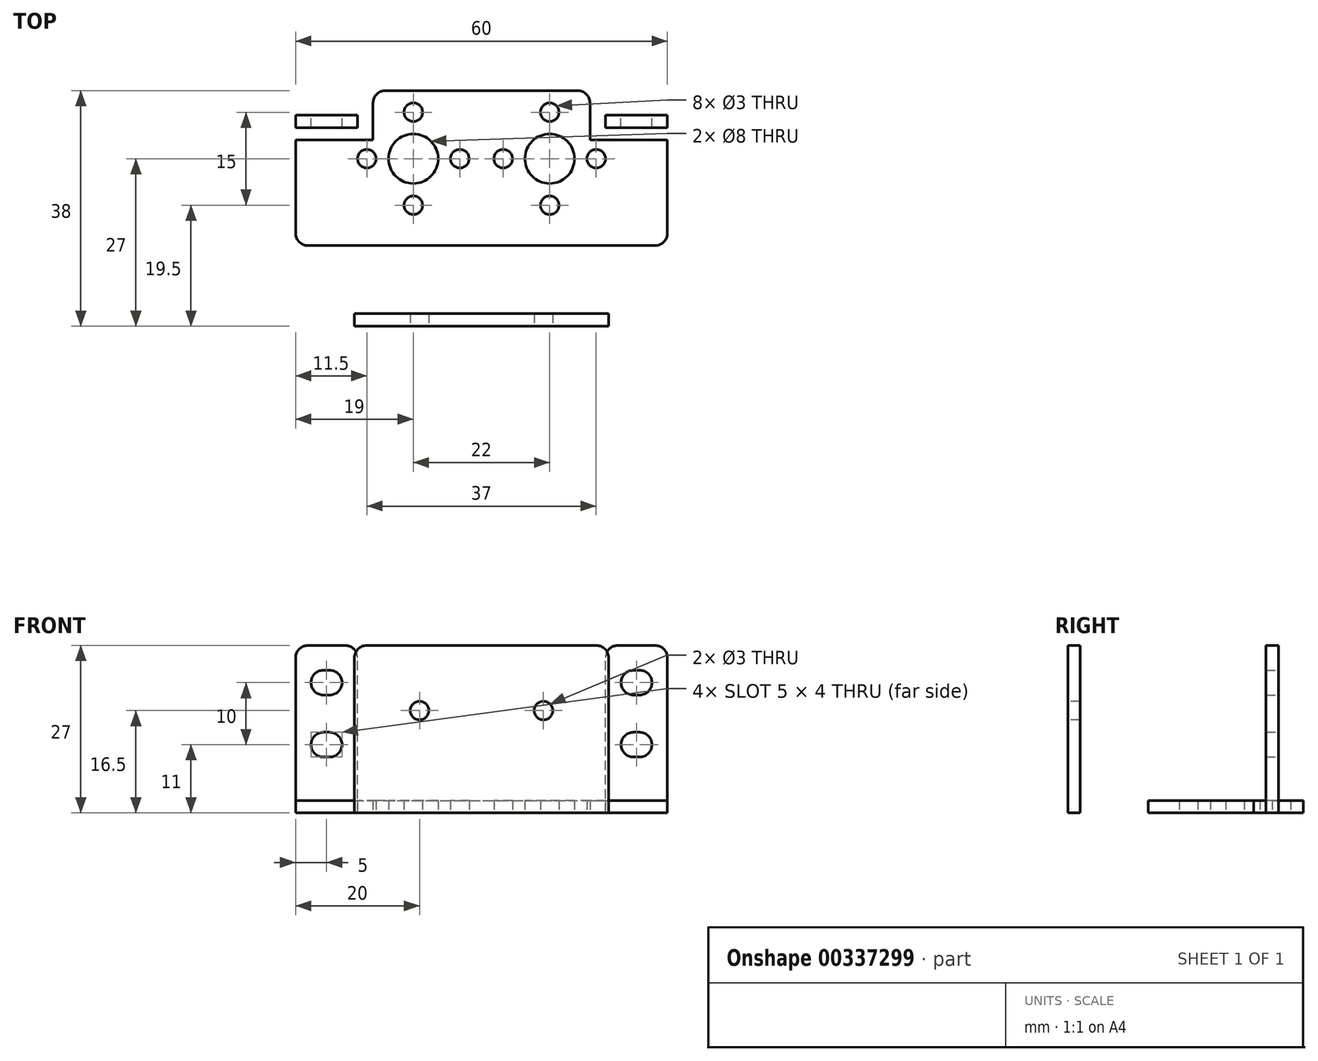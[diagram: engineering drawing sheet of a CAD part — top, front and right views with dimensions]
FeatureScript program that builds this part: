
annotation { "Feature Type Name" : "Feature", "Feature Type Description" : "" }
export const myFeature = defineFeature(function(context is Context, id is Id, definition is map)
    precondition{}
    {
        {
            var Q0;
            Q0=qCreatedBy(makeId("Top.planeOp"),FACE);
            var sketch = newSketch(context, id + "F0", { "sketchPlane" : qUnion([Q0])});
            skLineSegment(sketch, "E0.bottom", {"start": v(-17.5, 25) * mm, "end": v(17.5, 25) * mm});
            skLineSegment(sketch, "E0.top", {"start": v(-17.5, 17) * mm, "end": v(17.5, 17) * mm});
            skLineSegment(sketch, "E0.left", {"start": v(-17.5, 25) * mm, "end": v(-17.5, 17) * mm});
            skLineSegment(sketch, "E0.right", {"start": v(17.5, 25) * mm, "end": v(17.5, 17) * mm});
            skLineSegment(sketch, "E1.bottom", {"start": v(-30, 17) * mm, "end": v(30, 17) * mm});
            skLineSegment(sketch, "E1.top", {"start": v(-30, 0) * mm, "end": v(30, 0) * mm});
            skLineSegment(sketch, "E1.left", {"start": v(-30, 17) * mm, "end": v(-30, 0) * mm});
            skLineSegment(sketch, "E1.right", {"start": v(30, 17) * mm, "end": v(30, 0) * mm});
            skLineSegment(sketch, "E2.bottom", {"start": v(-20.5, 0) * mm, "end": v(20.5, 0) * mm});
            skLineSegment(sketch, "E2.top", {"start": v(-20.5, -13) * mm, "end": v(20.5, -13) * mm});
            skLineSegment(sketch, "E2.left", {"start": v(-20.5, 0) * mm, "end": v(-20.5, -13) * mm});
            skLineSegment(sketch, "E2.right", {"start": v(20.5, 0) * mm, "end": v(20.5, -13) * mm});
            skLineSegment(sketch, "E3.bottom", {"start": v(-30, 17) * mm, "end": v(-20, 17) * mm});
            skLineSegment(sketch, "E3.top", {"start": v(-30, 21) * mm, "end": v(-20, 21) * mm});
            skLineSegment(sketch, "E3.left", {"start": v(-30, 17) * mm, "end": v(-30, 21) * mm});
            skLineSegment(sketch, "E3.right", {"start": v(-20, 17) * mm, "end": v(-20, 21) * mm});
            skLineSegment(sketch, "E4.bottom", {"start": v(30, 17) * mm, "end": v(20, 17) * mm});
            skLineSegment(sketch, "E4.top", {"start": v(30, 21) * mm, "end": v(20, 21) * mm});
            skLineSegment(sketch, "E4.left", {"start": v(30, 17) * mm, "end": v(30, 21) * mm});
            skLineSegment(sketch, "E4.right", {"start": v(20, 17) * mm, "end": v(20, 21) * mm});
            skCircle(sketch, "E5", {"center": v(-11, 14) * mm, "radius": 4 * mm});
            skCircle(sketch, "E6", {"center": v(-11, 21.5) * mm, "radius": 1.5 * mm});
            skCircle(sketch, "E7", {"center": v(-3.5, 14) * mm, "radius": 1.5 * mm});
            skCircle(sketch, "E8", {"center": v(-11, 6.5) * mm, "radius": 1.5 * mm});
            skCircle(sketch, "E9", {"center": v(-18.5, 14) * mm, "radius": 1.5 * mm});
            skCircle(sketch, "E10", {"center": v(11, 14) * mm, "radius": 4 * mm});
            skCircle(sketch, "E11", {"center": v(11, 21.5) * mm, "radius": 1.5 * mm});
            skCircle(sketch, "E12", {"center": v(18.5, 14) * mm, "radius": 1.5 * mm});
            skCircle(sketch, "E13", {"center": v(11, 6.5) * mm, "radius": 1.5 * mm});
            skCircle(sketch, "E14", {"center": v(3.5, 14) * mm, "radius": 1.5 * mm});
            skPoint(sketch, "E15", {"position": v(0, 25) * mm});
            skSolve(sketch);
        }
        {
            var Q0;
            Q0=sQuery(id+"F0.wireOp",EDGE,"E2.top");
            var Q1;
            Q1=qCreatedBy(makeId("Front.planeOp"),FACE);
            cPlane(context, id + "F1", {"entities" : qUnion([Q0, Q1]), "cplaneType" : CPlaneType.LINE_ANGLE, "offset" : 25.4 * mm, "angle" : 0 * degree, "width" : 152.4 * mm, "height" : 152.4 * mm});
        }
        {
            var Q0;
            Q0=sQuery(id+"F0.wireOp",EDGE,"E4.top");
            var Q1;
            Q1=qCreatedBy(makeId("Front.planeOp"),FACE);
            cPlane(context, id + "F2", {"entities" : qUnion([Q0, Q1]), "cplaneType" : CPlaneType.LINE_ANGLE, "offset" : 25.4 * mm, "angle" : 0 * degree, "width" : 152.4 * mm, "height" : 152.4 * mm});
        }
        {
            var Q0;
            Q0=sQuery(id+"F0.wireOp",EDGE,"E3.top");
            var Q1;
            Q1=qCreatedBy(makeId("Front.planeOp"),FACE);
            cPlane(context, id + "F3", {"entities" : qUnion([Q0, Q1]), "cplaneType" : CPlaneType.LINE_ANGLE, "offset" : 25.4 * mm, "angle" : 0 * degree, "width" : 152.4 * mm, "height" : 152.4 * mm});
        }
        {
            var Q0;
            Q0=qCreatedBy(id+"F1.planeOp",FACE);
            var sketch = newSketch(context, id + "F4", { "sketchPlane" : qUnion([Q0])});
            skLineSegment(sketch, "E16.bottom", {"start": v(20.5, 0) * mm, "end": v(-20.5, 0) * mm});
            skLineSegment(sketch, "E16.top", {"start": v(20.5, 27) * mm, "end": v(-20.5, 27) * mm});
            skLineSegment(sketch, "E16.left", {"start": v(20.5, 0) * mm, "end": v(20.5, 27) * mm});
            skLineSegment(sketch, "E16.right", {"start": v(-20.5, 0) * mm, "end": v(-20.5, 27) * mm});
            skCircle(sketch, "E17", {"center": v(10, 16.5) * mm, "radius": 1.5 * mm});
            skCircle(sketch, "E18.MirrorC", {"center": v(-10, 16.5) * mm, "radius": 1.5 * mm});
            skSolve(sketch);
        }
        {
            var Q0;
            Q0=qCreatedBy(id+"F2.planeOp",FACE);
            var sketch = newSketch(context, id + "F5", { "sketchPlane" : qUnion([Q0])});
            skLineSegment(sketch, "E19.bottom", {"start": v(-30, 0) * mm, "end": v(-20, 0) * mm});
            skLineSegment(sketch, "E19.top", {"start": v(-30, 27) * mm, "end": v(-20, 27) * mm});
            skLineSegment(sketch, "E19.left", {"start": v(-30, 0) * mm, "end": v(-30, 27) * mm});
            skLineSegment(sketch, "E19.right", {"start": v(-20, 0) * mm, "end": v(-20, 27) * mm});
            skLineSegment(sketch, "E20.bottom", {"start": v(-25.5, 23) * mm, "end": v(-24.5, 23) * mm});
            skLineSegment(sketch, "E20.top", {"start": v(-25.5, 19) * mm, "end": v(-24.5, 19) * mm});
            skLineSegment(sketch, "E20.left", {"start": v(-25.5, 23) * mm, "end": v(-25.5, 19) * mm});
            skLineSegment(sketch, "E20.right", {"start": v(-24.5, 23) * mm, "end": v(-24.5, 19) * mm});
            skArc(sketch, "E21", {"start": v(-25.5, 23) * mm, "mid": v(-27.5, 21) * mm, "end": v(-25.5, 19) * mm});
            skArc(sketch, "E22", {"start": v(-24.5, 19) * mm, "mid": v(-22.5, 21) * mm, "end": v(-24.5, 23) * mm});
            skPoint(sketch, "E23", {"position": v(-25, 21) * mm});
            skPoint(sketch, "E24", {"position": v(-25, 27) * mm});
            skPoint(sketch, "E25", {"position": v(-25, 23) * mm});
            skLineSegment(sketch, "E26.bottom", {"start": v(-25.5, 13) * mm, "end": v(-24.5, 13) * mm});
            skLineSegment(sketch, "E26.top", {"start": v(-25.5, 9) * mm, "end": v(-24.5, 9) * mm});
            skLineSegment(sketch, "E26.left", {"start": v(-25.5, 13) * mm, "end": v(-25.5, 9) * mm});
            skLineSegment(sketch, "E26.right", {"start": v(-24.5, 13) * mm, "end": v(-24.5, 9) * mm});
            skArc(sketch, "E27", {"start": v(-25.5, 13) * mm, "mid": v(-27.5, 11) * mm, "end": v(-25.5, 9) * mm});
            skArc(sketch, "E28", {"start": v(-24.5, 9) * mm, "mid": v(-22.5, 11) * mm, "end": v(-24.5, 13) * mm});
            skPoint(sketch, "E29", {"position": v(-25, 11) * mm});
            skPoint(sketch, "E30", {"position": v(-25, 13) * mm});
            skSolve(sketch);
        }
        {
            var Q0;
            Q0=qCreatedBy(id+"F3.planeOp",FACE);
            var sketch = newSketch(context, id + "F6", { "sketchPlane" : qUnion([Q0])});
            skLineSegment(sketch, "E31.bottom", {"start": v(20, 0) * mm, "end": v(30, 0) * mm});
            skLineSegment(sketch, "E31.top", {"start": v(20, 27) * mm, "end": v(30, 27) * mm});
            skLineSegment(sketch, "E31.left", {"start": v(20, 0) * mm, "end": v(20, 27) * mm});
            skLineSegment(sketch, "E31.right", {"start": v(30, 0) * mm, "end": v(30, 27) * mm});
            skLineSegment(sketch, "E32.bottom", {"start": v(24.5, 23) * mm, "end": v(25.5, 23) * mm});
            skLineSegment(sketch, "E32.top", {"start": v(24.5, 19) * mm, "end": v(25.5, 19) * mm});
            skLineSegment(sketch, "E32.left", {"start": v(24.5, 23) * mm, "end": v(24.5, 19) * mm});
            skLineSegment(sketch, "E32.right", {"start": v(25.5, 23) * mm, "end": v(25.5, 19) * mm});
            skArc(sketch, "E33", {"start": v(24.5, 23) * mm, "mid": v(22.5, 21) * mm, "end": v(24.5, 19) * mm});
            skArc(sketch, "E34", {"start": v(25.5, 19) * mm, "mid": v(27.5, 21) * mm, "end": v(25.5, 23) * mm});
            skPoint(sketch, "E35", {"position": v(25, 21) * mm});
            skPoint(sketch, "E36", {"position": v(25, 27) * mm});
            skPoint(sketch, "E37", {"position": v(25, 23) * mm});
            skLineSegment(sketch, "E38.bottom", {"start": v(24.5, 13) * mm, "end": v(25.5, 13) * mm});
            skLineSegment(sketch, "E38.top", {"start": v(24.5, 9) * mm, "end": v(25.5, 9) * mm});
            skLineSegment(sketch, "E38.left", {"start": v(24.5, 13) * mm, "end": v(24.5, 9) * mm});
            skLineSegment(sketch, "E38.right", {"start": v(25.5, 13) * mm, "end": v(25.5, 9) * mm});
            skArc(sketch, "E39", {"start": v(24.5, 13) * mm, "mid": v(22.5, 11) * mm, "end": v(24.5, 9) * mm});
            skArc(sketch, "E40", {"start": v(25.5, 9) * mm, "mid": v(27.5, 11) * mm, "end": v(25.5, 13) * mm});
            skPoint(sketch, "E41", {"position": v(25, 11) * mm});
            skPoint(sketch, "E42", {"position": v(25, 13) * mm});
            skSolve(sketch);
        }
        {
            var Q0;
            {var subQ1=sQuery(id+"F0.wireOp",EDGE,"E1.left");Q0=makeQuery(id+"F0.imprint","IMPRINT",FACE,{"disambiguationData":[TD([[makeQuery(id+"F0.imprint","IMPRINT",EDGE,{"derivedFrom":subQ1}),1.0]])]});}
            var Q1;
            Q1=makeQuery(id+"F0.imprint","IMPRINT",FACE,{"disambiguationData":[TD([[makeQuery(id+"F0.imprint","IMPRINT",EDGE,{"derivedFrom":sQuery(id+"F0.wireOp",EDGE,"E0.bottom")}),-1.0]])]});
            var Q2;
            Q2=makeQuery(id+"F0.imprint","IMPRINT",FACE,{"disambiguationData":[TD([[makeQuery(id+"F0.imprint","IMPRINT",EDGE,{"derivedFrom":sQuery(id+"F0.wireOp",EDGE,"E2.bottom")}),-1.0]])]});
            var Q3;
            Q3=makeQuery(id+"F0.imprint","IMPRINT",FACE,{"disambiguationData":[TD([[makeQuery(id+"F0.imprint","IMPRINT",EDGE,{"derivedFrom":sQuery(id+"F0.wireOp",EDGE,"E4.bottom")}),-1.0]])]});
            var Q4;
            Q4=makeQuery(id+"F0.imprint","IMPRINT",FACE,{"disambiguationData":[TD([[makeQuery(id+"F0.imprint","IMPRINT",EDGE,{"derivedFrom":sQuery(id+"F0.wireOp",EDGE,"E3.bottom")}),1.0]])]});
            extrude(context, id + "F7", {"entities" : qUnion([Q0, Q1, Q2, Q3, Q4]), "depth" : 2 * mm});
        }
        {
            var Q0;
            Q0=makeQuery(id+"F4.imprint","IMPRINT",FACE,{"disambiguationData":[TD([[makeQuery(id+"F4.imprint","IMPRINT",EDGE,{"derivedFrom":sQuery(id+"F4.wireOp",EDGE,"E16.bottom")}),-1.0]])]});
            extrude(context, id + "F8", {"entities" : qUnion([Q0]), "operationType" : NewBodyOperationType.ADD, "depth" : 2 * mm});
        }
        {
            var Q0;
            Q0=makeQuery(id+"F6.imprint","IMPRINT",FACE,{"disambiguationData":[TD([[makeQuery(id+"F6.imprint","IMPRINT",EDGE,{"derivedFrom":sQuery(id+"F6.wireOp",EDGE,"E31.bottom")}),1.0]])]});
            var Q1;
            Q1=makeQuery(id+"F5.imprint","IMPRINT",FACE,{"disambiguationData":[TD([[makeQuery(id+"F5.imprint","IMPRINT",EDGE,{"derivedFrom":sQuery(id+"F5.wireOp",EDGE,"E19.bottom")}),1.0]])]});
            extrude(context, id + "F9", {"entities" : qUnion([Q0, Q1]), "operationType" : NewBodyOperationType.ADD, "oppositeDirection" : true, "depth" : 2 * mm});
        }
        {
            var Q0;
            Q0=makeQuery(id+"F7.opExtrude","CAP_EDGE",EDGE,{"disambiguationData":[OSD([sQuery(id+"F0.wireOp",EDGE,"E2.top")])],"isStart":true});
            var Q1;
            Q1=makeQuery(id+"F7.opExtrude","SWEPT_EDGE",EDGE,{"disambiguationData":[OSD([sQuery(id+"F0.wireOp",EDGE,"E1.top"),sQuery(id+"F0.wireOp",EDGE,"E1.left")])]});
            var Q2;
            Q2=makeQuery(id+"F7.opExtrude","SWEPT_EDGE",EDGE,{"disambiguationData":[OSD([sQuery(id+"F0.wireOp",EDGE,"E1.top"),sQuery(id+"F0.wireOp",EDGE,"E1.right")])]});
            var Q3;
            Q3=makeQuery(id+"F7.opExtrude","CAP_EDGE",EDGE,{"disambiguationData":[OSD([sQuery(id+"F0.wireOp",EDGE,"E4.top")])],"isStart":true});
            var Q4;
            Q4=makeQuery(id+"F7.opExtrude","CAP_EDGE",EDGE,{"disambiguationData":[OSD([sQuery(id+"F0.wireOp",EDGE,"E3.top")])],"isStart":true});
            var Q5;
            Q5=makeQuery(id+"F7.opExtrude","SWEPT_EDGE",EDGE,{"disambiguationData":[OSD([sQuery(id+"F0.wireOp",EDGE,"E0.bottom"),sQuery(id+"F0.wireOp",EDGE,"E0.right")])]});
            var Q6;
            Q6=makeQuery(id+"F7.opExtrude","SWEPT_EDGE",EDGE,{"disambiguationData":[OSD([sQuery(id+"F0.wireOp",EDGE,"E0.bottom"),sQuery(id+"F0.wireOp",EDGE,"E0.left")])]});
            var Q7;
            Q7=makeQuery(id+"F9.opExtrude","SWEPT_EDGE",EDGE,{"disambiguationData":[OSD([sQuery(id+"F5.wireOp",EDGE,"E19.top"),sQuery(id+"F5.wireOp",EDGE,"E19.left")])]});
            var Q8;
            Q8=makeQuery(id+"F9.opExtrude","SWEPT_EDGE",EDGE,{"disambiguationData":[OSD([sQuery(id+"F5.wireOp",EDGE,"E19.top"),sQuery(id+"F5.wireOp",EDGE,"E19.right")])]});
            var Q9;
            Q9=makeQuery(id+"F9.opExtrude","SWEPT_EDGE",EDGE,{"disambiguationData":[OSD([sQuery(id+"F6.wireOp",EDGE,"E31.top"),sQuery(id+"F6.wireOp",EDGE,"E31.left")])]});
            var Q10;
            Q10=makeQuery(id+"F9.opExtrude","SWEPT_EDGE",EDGE,{"disambiguationData":[OSD([sQuery(id+"F6.wireOp",EDGE,"E31.top"),sQuery(id+"F6.wireOp",EDGE,"E31.right")])]});
            var Q11;
            Q11=makeQuery(id+"F8.opExtrude","SWEPT_EDGE",EDGE,{"disambiguationData":[OSD([sQuery(id+"F4.wireOp",EDGE,"E16.top"),sQuery(id+"F4.wireOp",EDGE,"E16.left")])]});
            var Q12;
            Q12=makeQuery(id+"F8.opExtrude","SWEPT_EDGE",EDGE,{"disambiguationData":[OSD([sQuery(id+"F4.wireOp",EDGE,"E16.top"),sQuery(id+"F4.wireOp",EDGE,"E16.right")])]});
            fillet(context, id + "F10", {"entities" : qUnion([Q0, Q1, Q2, Q3, Q4, Q5, Q6, Q7, Q8, Q9, Q10, Q11, Q12]), "radius" : 2 * mm, "tangentPropagation" : true, "allowEdgeOverflow" : false});
        }
    });
